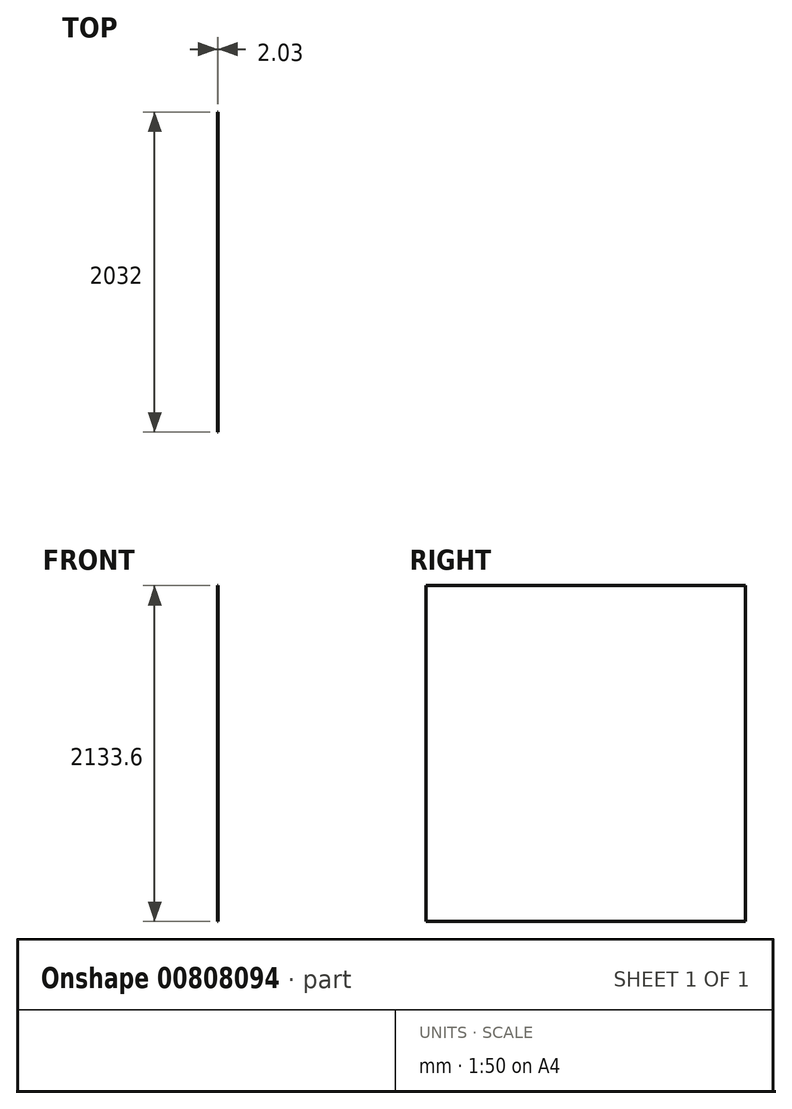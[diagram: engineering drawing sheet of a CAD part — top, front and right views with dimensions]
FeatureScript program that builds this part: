
annotation { "Feature Type Name" : "Feature", "Feature Type Description" : "" }
export const myFeature = defineFeature(function(context is Context, id is Id, definition is map)
    precondition{}
    {
        {
            var Q0;
            Q0=qCreatedBy(makeId("Front.planeOp"),FACE);
            var sketch = newSketch(context, id + "F0", { "sketchPlane" : qUnion([Q0])});
            skLineSegment(sketch, "E0.right", {"start": v(-3294.89, 1462.86) * mm, "end": v(-3294.89, -670.74) * mm});
            skLineSegment(sketch, "E1.left", {"start": v(-3294.89, -256.4) * mm, "end": v(-3294.89, -267.6) * mm});
            skLineSegment(sketch, "E2.left", {"start": v(-3294.89, -525.16) * mm, "end": v(-3294.89, -513.96) * mm});
            skLineSegment(sketch, "E3", {"start": v(-3294.89, 1462.86) * mm, "end": v(-3292.86, 1462.86) * mm});
            skLineSegment(sketch, "E4", {"start": v(-3292.86, 1462.86) * mm, "end": v(-3292.86, -670.74) * mm});
            skLineSegment(sketch, "E5", {"start": v(-3292.86, -670.74) * mm, "end": v(-3294.89, -670.74) * mm});
            skSolve(sketch);
        }
        {
            var Q0;
            Q0=qSketchRegion(id+"F0",true);
            extrude(context, id + "F1", {"entities" : qUnion([Q0]), "depth" : 2032 * mm, "offsetDistance" : 25.4 * mm});
        }
    });
